# Revit family: 2019_ES_Ventana_Qsystems_Q77+_1-Hoja_Fija
name_source: partatom
category: Windows
units: mm (PartAtom-declared; Revit-internal decimal feet)

## family parameters
Always vertical = Yes
Cut with Voids When Loaded = No
Host = Wall
OmniClass Number = 23.30.20.00
OmniClass Title = Windows
Room Calculation Point = No
Shared = No

## types (1)
- 600x1000 mm
    Acabado = Anodizado, lacado y acabados
    AcidificacionAtmosferica = 0
    AcidificacionAtmosfericaPorUnidad = 0
    Acristalamiento = Cristal - Vidrio claro templado
    AguaConsumida = 0
    AguaConsumidaPorUnidad = 0
    Altura Máxima = 5000 mm  [stored 16.4042 ft]
    Altura Real = 1000 mm  [stored 3.28084 ft]
    Altura de antepecho por defecto = 800 mm
    Altura maxima = 2500 mm  [stored 8.2021 ft]
    Altura minima = 600 mm  [stored 1.9685 ft]
    Analytic Construction = <None>
    AnchoPoliamidaHoja = 30 mm  [stored 0.0984252 ft]
    AnchoPoliamidaMarco = 30 mm  [stored 0.0984252 ft]
    Anchura Maxima = 1700 mm  [stored 5.57743 ft]
    Anchura Minima = 100 mm  [stored 0.328084 ft]
    Anchura Máxima = 5000 mm  [stored 16.4042 ft]
    Anchura Real = 600 mm  [stored 1.9685 ft]
    Area = 600000 mm²
    Autor = Bimetica Parametric Design Services, S.L.
    BIMsupport = https://bimsupport.info
    COBieCategoria = IfcWindow
    CambioClimatico = 0
    CambioClimaticoPorUnidad = 0
    Catálogo (URL) = https://qsystemsaluminio.com
    CerramientoExterior = Yes
    Clasificacion acustica = 45 (-2,-6) dB
    ConfiguracionPoliamidas = 273800 - 493700
    ControlHumos = No
    CosteEnergeticoKwh = 0
    CosteEnergeticoMj = 0 J
    CosteMantenimiento = 0
    Description = Ventana Fija
    Desfase Acristalamiento = 5.25 mm  [stored 0.0172244 ft]
    DestruccionCapaOzonoEstratosferica = 0
    DestruccionCapaOzonoEstratosfericaPorUnidad = 0
    Detalle Perfileria = Yes
    EmisionCO2 = 0
    Energia consumida = 0
    EnergiaNoRenovableConsumida = 0
    EnergiaNoRenovableConsumidaPorUnidad = 0
    EnergiaPrimariaTotalConsumida = 0
    EnergiaPrimariaTotalConsumidaPorUnidad = 0
    EnergiaRenovableConsumida = 0
    EnergiaRenovableConsumidaPorUnidad = 0
    EstanqueidadAgua = E1650
    Eutrofizacion = 0
    EutrofizacionPorUnidad = 0
    FactorSolarModificado = 0
    FactorSombra = 0
    FaltaDeRecursos = 0
    FaltaDeRecursosPorUnidad = 0
    FechaEmisionElementoBIM = 03/12/2021
    FechaVencimientoElementoBIM = 03/12/2022
    FormacionFotoquimicaOzono = 0
    FormacionFotoquimicaOzonoPorUnidad = 0
    Fraccion de area de acristalamiento = 0.659333
    GrosorAcristalamiento = 32 mm  [stored 0.104987 ft]
    GrosorMarco = 70 mm  [stored 0.229659 ft]
    GrosorMaximoAcristalamiento = 0 mm  [stored 0 ft]
    GrosorMinimoAcristalamiento = 0 mm  [stored 0 ft]
    Gubimclass Codigo = 30.10.20.10
    Gubimclass Titulo = Ventanas de fachadas
    Height = 1000 mm  [stored 3.28084 ft]
    Historial = (RVT2019) Actualziación a estándar GDO-BIM y datos. (RVT2015) Creación del Elemento.
    IfcExportAs = IfcWindow
    IfcExportType = Hoja Fija
    Infiltracion = 0
    InformacionTecnica = http://www.alueuropa.com
    Manufacturer = QSystems
    Marcado CE = No
    Marco = Aluminio Anodizado, lacado
    MasterformatCodigo = 08 51 13
    MasterformatTitulo = Aluminium Windows
    Model = Q77+
    Motorizada = No
    Numero de Licencia = XXX-XXXX9536
    OmniclassCodigo = 23-17 13 00
    OmniclassTitulo = Windows
    Operation = Fija
    Perimetro = 3200
    PermeabilidadAlAire = Clase 4
    Peso = 0.00 kg
    Plataforma descaga contenido BIM = www.bimetica.com
    Poliamida = Technoform polyamide
    Profundidad = 0 mm  [stored 0 ft]
    PuntoDeContacto = QSystems
    Referencia = Q77+
    ReferenciaContacto = QSystems
    RepisaExterior = Yes
    RepisaInterior = Yes
    ResiduoInerte = 0
    ResiduoInertePorUnidad = 0
    ResiduoRadioactivo = 0
    ResiduoRadioactivoPorUnidad = 0
    ResiduosNoPeligrosos = 0
    ResiduosNoPeligrososPorUnidad = 0
    ResiduosPeligrosos = 0
    ResiduosPeligrososPorUnidad = 0
    ResistenciaAlViento = Clase C5
    Rough Height = 605 mm
    Rough Width = 1005 mm  [stored 3.29724 ft]
    SalidaEmergencia = No
    Serie = Q77+
    TelefonoContacto = +34 91 895 58 00
    Titular = Alueuropa S.A.
    Transmitancia termica = 0 W/(m²·K)
    TransmitanciaTermica = 0 W/(m²·K)
    Type Comments = Sistema de Ventana Q77  Fija
    UNSPSCCodigo = 30171600
    UNSPSCTitulo = Windows
    URL = http://www.alueuropa.com
    URL Perfil BIM = https://bimetica.com
    URL Poliamida = http://www.technoform.es
    URL Poliamida - Catálogo = http://www.technoform.com
    URLProducto = https://qsystemsaluminio.com
    Uniclass2.0Codigo = 25-30
    Uniclass2.0Titulo = Door and window systems
    Version = RVT2019
    Version Estandar GDO-BIM = GDO-BIM V02
    Wall Closure = By host
    Width = 600 mm  [stored 1.9685 ft]
    Y𝑔 = 0.11
    𝐴𝑓 = 150000
    𝐴𝑔 = 450000
    𝑈𝑓 = 3.629
    𝑈𝑔 = 1.9
    𝑈𝑤 = 2.845583
    𝑙𝑔 = 2800

note: [stored X ft] marks values corroborated as IEEE doubles in the binary element streams (Revit-internal decimal feet)

## geometry (parser evidence)
native form markers: Blend x2
no freeform markers — native parametric forms only
